# Revit family: Haworth_Orla_Armchair
name_source: partatom
category: Furniture
revit_build: Autodesk Revit 2018 (Build: 20170223_1515(x64)
units: mm (PartAtom-declared; Revit-internal decimal feet)

## family parameters
Always vertical = Yes
Cut with Voids When Loaded = No
OmniClass Number = 23.40.20.00
OmniClass Title = General Furniture and Specialties
Room Calculation Point = No
Shared = No
Work Plane-Based = No

## types (2) — shared parameters
Actual Depth = 2' - 8 3/4"
Actual Height = 1' - 11 1/4"
Actual Width = 2' - 9 3/4"
Assembly Code = E2020200
Description = Haworth Orla Armchair
Manufacturer = Haworth
Model = HCCE-ORL1
Size = Verify Final Dim. w/ Haworth
URL = http://www.haworth.com
URL - Product = http://www.haworth.com
Version = 3
Warranty = http://www.haworth.com

## per-type parameters (varying)
| type | Base Finish | Fixed Base | Swivel Base |
| HCCE-ORL1 - Swivel Base | Haworth _ Metal _ Brushed Aluminum | No | Yes |
| HCCE-ORL1 - Fixed Base | Haworth _ Polymer _ Black | Yes | No |

## geometry (parser evidence)
native form markers: Blend x8, Sweep x2
no freeform markers — native parametric forms only
